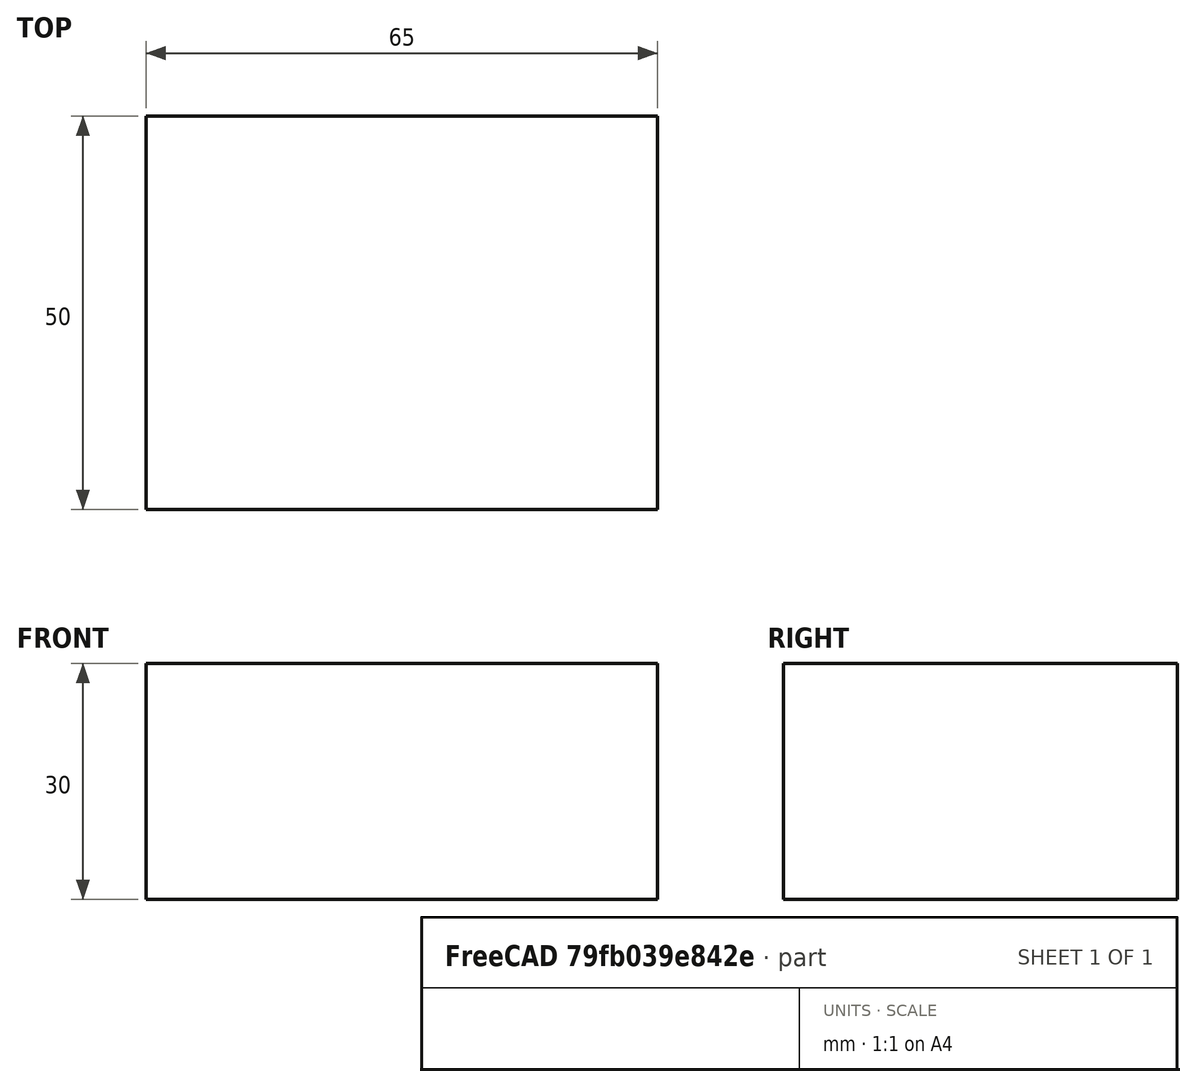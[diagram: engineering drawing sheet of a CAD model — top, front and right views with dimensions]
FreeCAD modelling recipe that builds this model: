
FCSTD DOCUMENT  (FreeCAD 0.16R6706 (Git))
Label: dock1
License: All rights reserved
LicenseURL: http://en.wikipedia.org/wiki/All_rights_reserved
objects: Sketcher::SketchObject×2, PartDesign::Pad×1
note: 4 computed .brp shape members not serialized (recipe doc carries the construction recipe); baked Part::Feature solids carry a one-line shape summary decoded from their .brp

FEATURE [Sketcher::SketchObject] Sketch
  sketch-geometry (10):
    g0: LineSegment StartX=0 StartY=0 StartZ=0 EndX=65 EndY=0 EndZ=0
    g1: LineSegment StartX=65 StartY=0 StartZ=0 EndX=65 EndY=50 EndZ=0
    g2: LineSegment StartX=65 StartY=50 StartZ=0 EndX=0 EndY=50 EndZ=0
    g3: LineSegment StartX=0 StartY=50 StartZ=0 EndX=0 EndY=0 EndZ=0
    g4: LineSegment [constr] StartX=2 StartY=1.32982 StartZ=0 EndX=63 EndY=1.32982 EndZ=0
    g5: LineSegment [constr] StartX=63 StartY=1.32982 StartZ=0 EndX=63 EndY=9.79214 EndZ=0
    g6: LineSegment [constr] StartX=63 StartY=9.79214 StartZ=0 EndX=2 EndY=9.79214 EndZ=0
    g7: LineSegment [constr] StartX=2 StartY=9.79214 StartZ=0 EndX=2 EndY=1.32982 EndZ=0
    g8: LineSegment [constr] StartX=2 StartY=9.79214 StartZ=0 EndX=0 EndY=9.79214 EndZ=0
    g9: LineSegment [constr] StartX=63 StartY=9.79214 StartZ=0 EndX=65 EndY=9.79214 EndZ=0
  constraints (28):
    c: Coincident(g0,g1)
    c: Coincident(g1,g2)
    c: Coincident(g2,g3)
    c: Coincident(g3,g0)
    c: Horizontal(g0)
    c: Horizontal(g2)
    c: Vertical(g1)
    c: Vertical(g3)
    c: PointOnObject(g0,g-2)
    c: Coincident(g0,g-1)
    c: Coincident(g4,g5)
    c: Coincident(g5,g6)
    c: Coincident(g6,g7)
    c: Coincident(g7,g4)
    c: Horizontal(g4)
    c: Horizontal(g6)
    c: Vertical(g5)
    c: Vertical(g7)
    c: DistanceX(g4,g4) = 61
    c: PointOnObject(g8,g3)
    c: Horizontal(g8)
    c: DistanceX(g8,g8) = 2
    c: Coincident(g8,g6)
    c: Coincident(g9,g5)
    c: PointOnObject(g9,g1)
    c: Horizontal(g9)
    c: Equal(g9,g8)
    c: DistanceY(g3,g3) = 50
FEATURE [PartDesign::Pad] Pad
  Length = 30
  Length2 = 100
  Sketch = -> Sketch
  Type = 0
FEATURE [Sketcher::SketchObject] Sketch001
  ExternalGeometry = -> [Pad]
  Placement = pos=(65,0,0) rot=(0.57735,0.57735,0.57735;2.0944rad)
  Support = -> Pad [Face2]
  sketch-geometry (3):
    g0: LineSegment StartX=0 StartY=0 StartZ=0 EndX=15.7468 EndY=30 EndZ=0
    g1: LineSegment StartX=0 StartY=30 StartZ=0 EndX=15.7468 EndY=30 EndZ=0
    g2: LineSegment StartX=0 StartY=30 StartZ=0 EndX=0 EndY=0 EndZ=0
  constraints (6):
    c: Coincident(g0,g-1)
    c: PointOnObject(g0,g-4)
    c: Coincident(g1,g-4)
    c: Coincident(g1,g0)
    c: Coincident(g2,g1)
    c: Coincident(g2,g-1)
